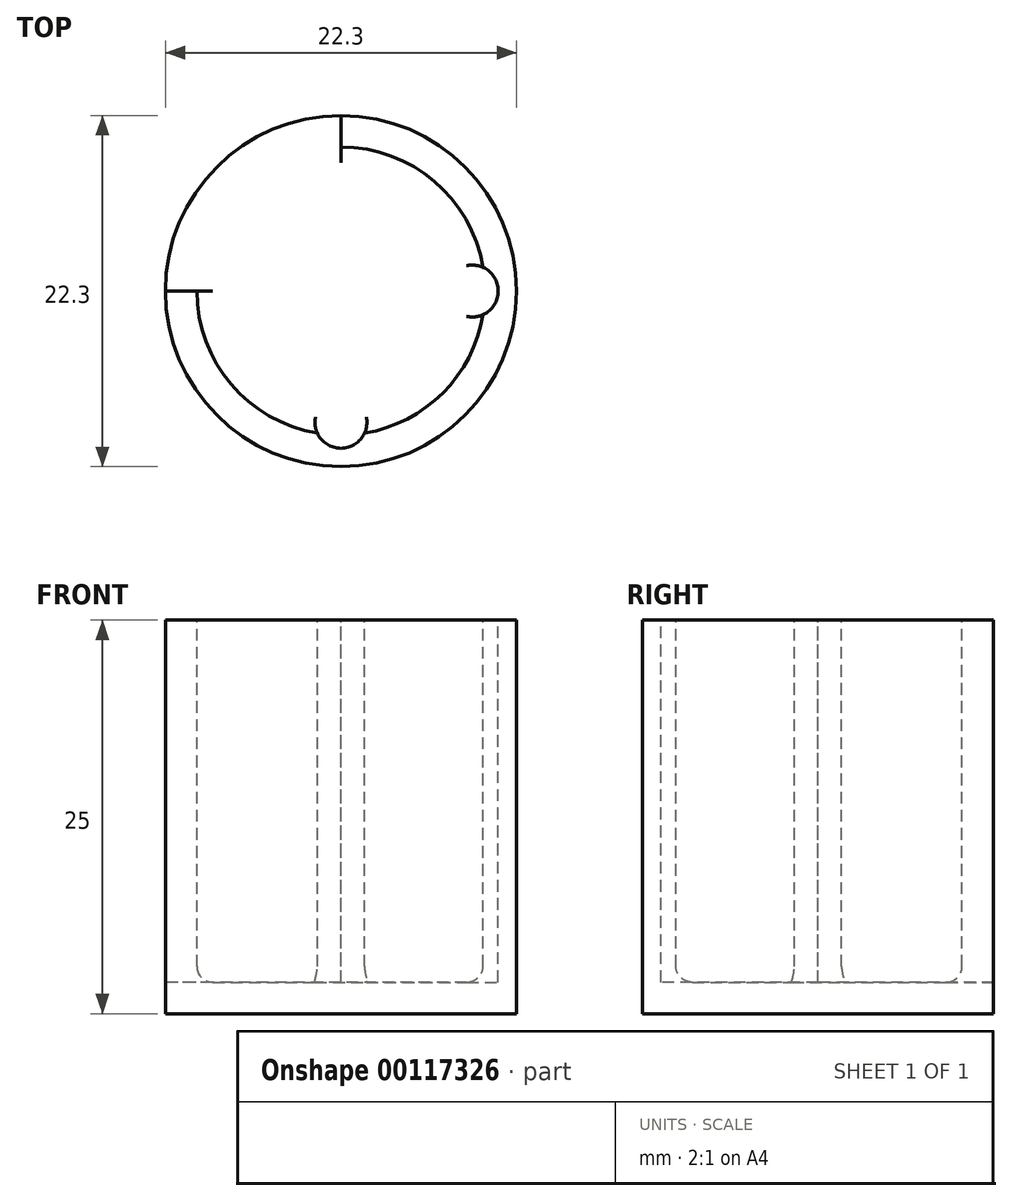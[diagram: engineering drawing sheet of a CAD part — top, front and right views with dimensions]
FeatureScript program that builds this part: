
annotation { "Feature Type Name" : "Feature", "Feature Type Description" : "" }
export const myFeature = defineFeature(function(context is Context, id is Id, definition is map)
    precondition{}
    {
        {
            var Q0;
            Q0=qCreatedBy(makeId("Top.planeOp"),FACE);
            var sketch = newSketch(context, id + "F0", { "sketchPlane" : qUnion([Q0])});
            skCircle(sketch, "E0", {"center": v(0, 0) * mm, "radius": 8.85 * mm, "construction": true});
            skCircle(sketch, "E1.0", {"center": v(0, 0) * mm, "radius": 11.15 * mm});
            skSolve(sketch);
        }
        {
            var Q0;
            Q0 = qSketchRegion(id + "F0", true);
            extrude(context, id + "F1", {"entities" : qUnion([Q0]), "depth" : 25 * mm});
        }
        {
            var Q0;
            Q0=makeQuery(id+"F1.opExtrude","CAP_FACE",FACE,{"disambiguationData":[OSD([sQuery(id+"F0.wireOp",EDGE,"E1.0")])],"isStart":false});
            var sketch = newSketch(context, id + "F2", { "sketchPlane" : qUnion([Q0])});
            skCircle(sketch, "E2.0", {"center": v(0, 0) * mm, "radius": 11.15 * mm, "construction": true});
            skCircle(sketch, "E3.0", {"center": v(0, 0) * mm, "radius": 9.15 * mm});
            skArc(sketch, "E4", {"start": v(9.03, -1.5) * mm, "mid": v(9.99, 0) * mm, "end": v(9.03, 1.5) * mm});
            skLineSegment(sketch, "E5", {"start": v(0, 0) * mm, "end": v(0, 9.15) * mm, "construction": true});
            skLineSegment(sketch, "E6", {"start": v(0, 0) * mm, "end": v(-9.15, 0) * mm, "construction": true});
            skLineSegment(sketch, "E7", {"start": v(0, 9.15) * mm, "end": v(0, 11.15) * mm});
            skLineSegment(sketch, "E8", {"start": v(-9.15, 0) * mm, "end": v(-11.15, 0) * mm});
            skLineSegment(sketch, "E9", {"start": v(0, 0) * mm, "end": v(0, -9.03) * mm, "construction": true});
            skArc(sketch, "E10", {"start": v(-1.5, -9.03) * mm, "mid": v(0, -9.99) * mm, "end": v(1.5, -9.03) * mm});
            skLineSegment(sketch, "E11", {"start": v(9.03, 1.5) * mm, "end": v(9.03, -1.5) * mm, "construction": true});
            skLineSegment(sketch, "E12", {"start": v(0, 0) * mm, "end": v(9.03, 0) * mm, "construction": true});
            skLineSegment(sketch, "E13", {"start": v(-1.5, -9.03) * mm, "end": v(1.5, -9.03) * mm, "construction": true});
            skSolve(sketch);
        }
        {
            var Q0;
            Q0 = qSketchRegion(id + "F2", true);
            var Q1;
            {var subQ0=sQuery(id+"F2.wireOp",EDGE,"E7");Q1=makeQuery(id+"F2.imprint","IMPRINT",FACE,{"disambiguationData":[TD([[makeQuery(id+"F2.imprint","IMPRINT",EDGE,{"derivedFrom":subQ0}),1.0]])]});}
            extrude(context, id + "F3", {"entities" : qUnion([Q0, Q1]), "operationType" : NewBodyOperationType.REMOVE, "oppositeDirection" : true, "depth" : 23 * mm});
        }
        {
            var Q0;
            {var subQ0=sQuery(id+"F2.wireOp",EDGE,"E3.0");Q0=makeQuery(id+"F3.boolean.opBoolean","COPY",EDGE,{"derivedFrom":makeQuery(id+"F3.opExtrude","CAP_EDGE",EDGE,{"disambiguationData":[OSD([subQ0]),TDD([makeQuery(id+"F2.imprint","IMPRINT",EDGE,{"disambiguationData":[TD([[makeQuery(id+"F2.imprint","INTERSECT",VERTEX,{"disambiguationData":[OD(1.0)],"derivedFrom":[subQ0,sQuery(id+"F2.wireOp",EDGE,"E4")]}),-1.0]])],"derivedFrom":subQ0})])],"isStart":false})});}
            var Q1;
            {var subQ0=sQuery(id+"F2.wireOp",EDGE,"E3.0");Q1=makeQuery(id+"F3.boolean.opBoolean","COPY",EDGE,{"derivedFrom":makeQuery(id+"F3.opExtrude","CAP_EDGE",EDGE,{"disambiguationData":[OSD([subQ0]),TDD([makeQuery(id+"F2.imprint","IMPRINT",EDGE,{"disambiguationData":[TD([[makeQuery(id+"F2.imprint","INTERSECT",VERTEX,{"disambiguationData":[OD(0.0)],"derivedFrom":[subQ0,sQuery(id+"F2.wireOp",EDGE,"E4")]}),1.0]])],"derivedFrom":subQ0})])],"isStart":false})});}
            var Q2;
            {var subQ0=sQuery(id+"F2.wireOp",EDGE,"E3.0");Q2=makeQuery(id+"F3.boolean.opBoolean","COPY",EDGE,{"derivedFrom":makeQuery(id+"F3.opExtrude","CAP_EDGE",EDGE,{"disambiguationData":[OSD([subQ0]),TDD([makeQuery(id+"F2.imprint","IMPRINT",EDGE,{"disambiguationData":[TD([[makeQuery(id+"F2.imprint","INTERSECT",VERTEX,{"derivedFrom":[subQ0,sQuery(id+"F2.wireOp",EDGE,"E8")]}),-1.0]])],"derivedFrom":subQ0})])],"isStart":false})});}
            var Q3;
            {var subQ0=sQuery(id+"F2.wireOp",EDGE,"E3.0");Q3=makeQuery(id+"F3.boolean.opBoolean","COPY",EDGE,{"derivedFrom":makeQuery(id+"F3.opExtrude","CAP_EDGE",EDGE,{"disambiguationData":[OSD([subQ0]),TDD([makeQuery(id+"F2.imprint","IMPRINT",EDGE,{"disambiguationData":[TD([[makeQuery(id+"F2.imprint","INTERSECT",VERTEX,{"disambiguationData":[OD(1.0)],"derivedFrom":[subQ0,sQuery(id+"F2.wireOp",EDGE,"E4")]}),-1.0]])],"derivedFrom":subQ0})])],"isStart":true})});}
            fillet(context, id + "F4", {"entities" : qUnion([Q0, Q1, Q2, Q3]), "radius" : 1 * mm, "tangentPropagation" : true, "allowEdgeOverflow" : false});
        }
    });
